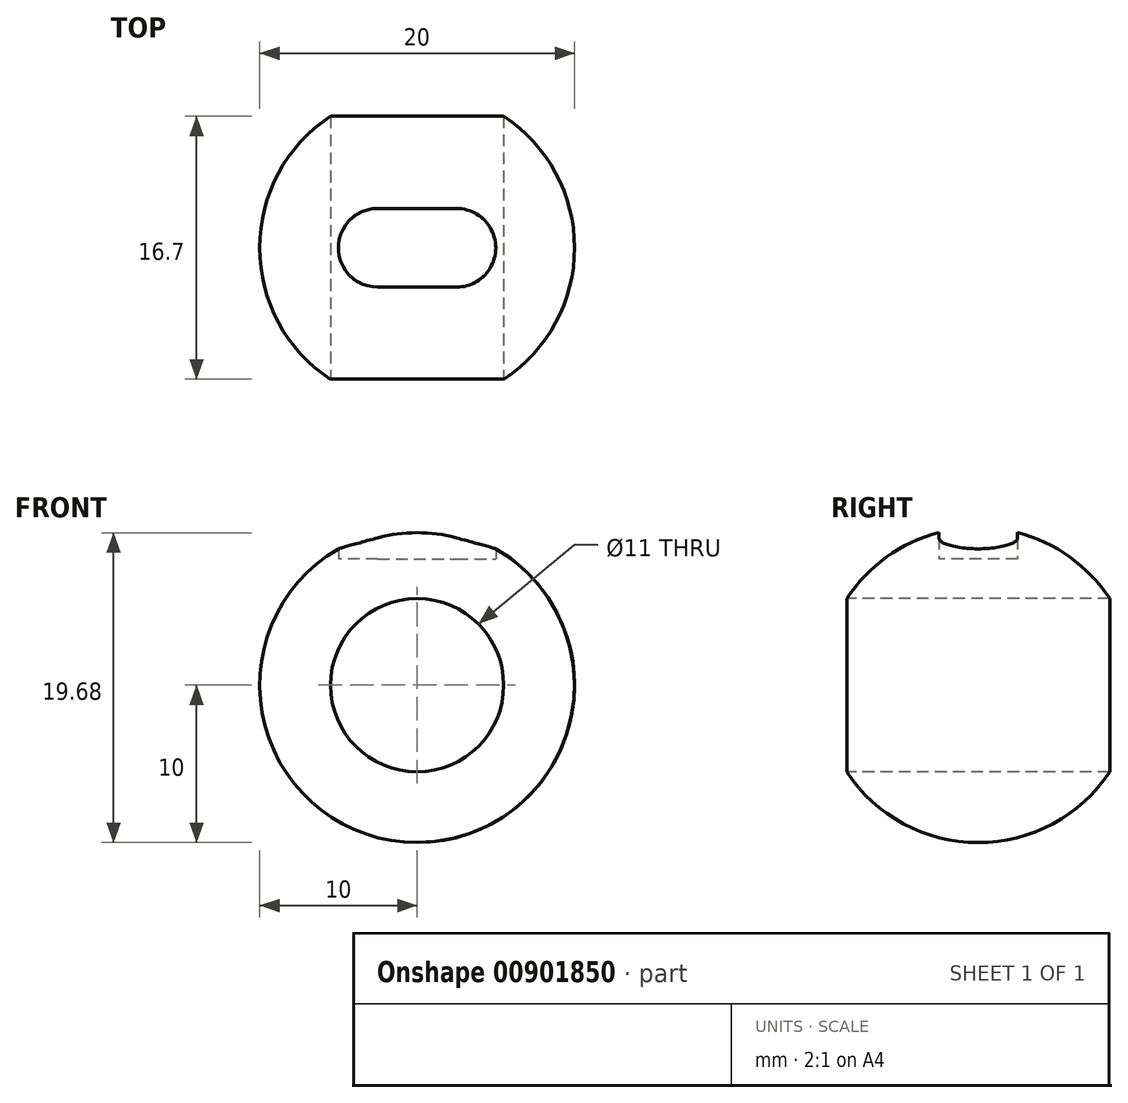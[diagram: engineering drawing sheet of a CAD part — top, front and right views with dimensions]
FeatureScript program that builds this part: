
annotation { "Feature Type Name" : "Feature", "Feature Type Description" : "" }
export const myFeature = defineFeature(function(context is Context, id is Id, definition is map)
    precondition{}
    {
        {
            var Q0;
            Q0=qCreatedBy(makeId("Front.planeOp"),FACE);
            var sketch = newSketch(context, id + "F0", { "sketchPlane" : qUnion([Q0])});
            skLineSegment(sketch, "E0", {"start": v(0, 10) * mm, "end": v(0, -10) * mm});
            skPoint(sketch, "E1", {"position": v(0, 0) * mm});
            skArc(sketch, "E2", {"start": v(0, -10) * mm, "mid": v(10, 0) * mm, "end": v(0, 10) * mm});
            skSolve(sketch);
        }
        {
            var Q0;
            Q0=makeQuery(id+"F0.imprint","IMPRINT",FACE,{"disambiguationData":[TD([[makeQuery(id+"F0.imprint","IMPRINT",EDGE,{"derivedFrom":sQuery(id+"F0.wireOp",EDGE,"E0")}),1.0]])]});
            var Q1;
            Q1=sQuery(id+"F0.wireOp",EDGE,"E2");
            var Q2;
            Q2=sQuery(id+"F0.wireOp",EDGE,"E0");
            revolve(context, id + "F1", {"surfaceOperationType" : NewSurfaceOperationType.ADD, "entities" : qUnion([Q0]), "surfaceEntities" : qUnion([Q1]), "axis" : qUnion([Q2]), "revolveType" : RevolveType.ONE_DIRECTION, "oppositeDirection" : true, "angle" : 180 * degree});
        }
        {
            var Q0;
            Q0=makeQuery(id+"F1.opRevolve","CAP_FACE",FACE,{"disambiguationData":[OSD([sQuery(id+"F0.wireOp",EDGE,"E0"),sQuery(id+"F0.wireOp",EDGE,"E2")])],"isStart":true});
            var sketch = newSketch(context, id + "F2", { "sketchPlane" : qUnion([Q0])});
            skCircle(sketch, "E3", {"center": v(0, 0) * mm, "radius": 5.5 * mm});
            skLineSegment(sketch, "E4", {"start": v(-2.5, 8) * mm, "end": v(2.5, 8) * mm});
            skPoint(sketch, "E5", {"position": v(0, 8) * mm});
            skArc(sketch, "E6", {"start": v(2.5, 8) * mm, "mid": v(3.59, 8.25) * mm, "end": v(4.46, 8.95) * mm});
            skArc(sketch, "E7.MirrorCS", {"start": v(-2.5, 8) * mm, "mid": v(-3.59, 8.25) * mm, "end": v(-4.46, 8.95) * mm});
            skSolve(sketch);
        }
        {
            var Q0;
            Q0=sQuery(id+"F2.wireOp",VERTEX,"E3.center");
            var Q1;
            Q1=makeQuery(id+"F1.opRevolve","SWEPT_BODY",BODY,{"disambiguationData":[OSD([sQuery(id+"F0.wireOp",EDGE,"E0"),sQuery(id+"F0.wireOp",EDGE,"E2")])]});
            hole(context, id + "F3", {"style" : HoleStyle.SIMPLE, "endStyle" : HoleEndStyle.THROUGH, "holeDiameter" : 11 * mm, "majorDiameter" : 5 * mm, "isTappedThrough" : true, "tappedDepth" : 12 * mm, "tapClearance" : 3, "locations" : qUnion([Q0]), "scope" : qUnion([Q1])});
        }
        {
            var Q0;
            Q0=makeQuery(id+"F1.opRevolve","SWEPT_BODY",BODY,{"disambiguationData":[OSD([sQuery(id+"F0.wireOp",EDGE,"E0"),sQuery(id+"F0.wireOp",EDGE,"E2")])]});
            var Q1;
            Q1=makeQuery(id+"F2.imprint","IMPRINT",FACE,{"disambiguationData":[TD([[makeQuery(id+"F2.imprint","IMPRINT",EDGE,{"derivedFrom":sQuery(id+"F2.wireOp",EDGE,"E3")}),1.0]])]});
            mirror(context, id + "F4", {"operationType" : NewBodyOperationType.ADD, "entities" : qUnion([Q0]), "mirrorPlane" : qUnion([Q1])});
        }
        {
            var Q0;
            Q0=qCreatedBy(makeId("Top.planeOp"),FACE);
            var sketch = newSketch(context, id + "F5", { "sketchPlane" : qUnion([Q0])});
            skLineSegment(sketch, "E8", {"start": v(-2.5, -2.5) * mm, "end": v(2.5, -2.5) * mm});
            skLineSegment(sketch, "E9", {"start": v(-2.5, 2.5) * mm, "end": v(2.5, 2.5) * mm});
            skPoint(sketch, "E10", {"position": v(0, 2.5) * mm});
            skPoint(sketch, "E11", {"position": v(0, -2.5) * mm});
            skArc(sketch, "E12", {"start": v(-2.5, 2.5) * mm, "mid": v(-5, 0) * mm, "end": v(-2.5, -2.5) * mm});
            skArc(sketch, "E13", {"start": v(2.5, 2.5) * mm, "mid": v(5, 0) * mm, "end": v(2.5, -2.5) * mm});
            skSolve(sketch);
        }
        {
            var Q0;
            Q0 = qSketchRegion(id + "F5", true);
            extrude(context, id + "F6", {"entities" : qUnion([Q0]), "operationType" : NewBodyOperationType.REMOVE, "depth" : 25 * mm, "offsetDistance" : 25 * mm, "hasSecondDirection" : true, "secondDirectionOppositeDirection" : false, "secondDirectionDepth" : 8 * mm});
        }
    });
